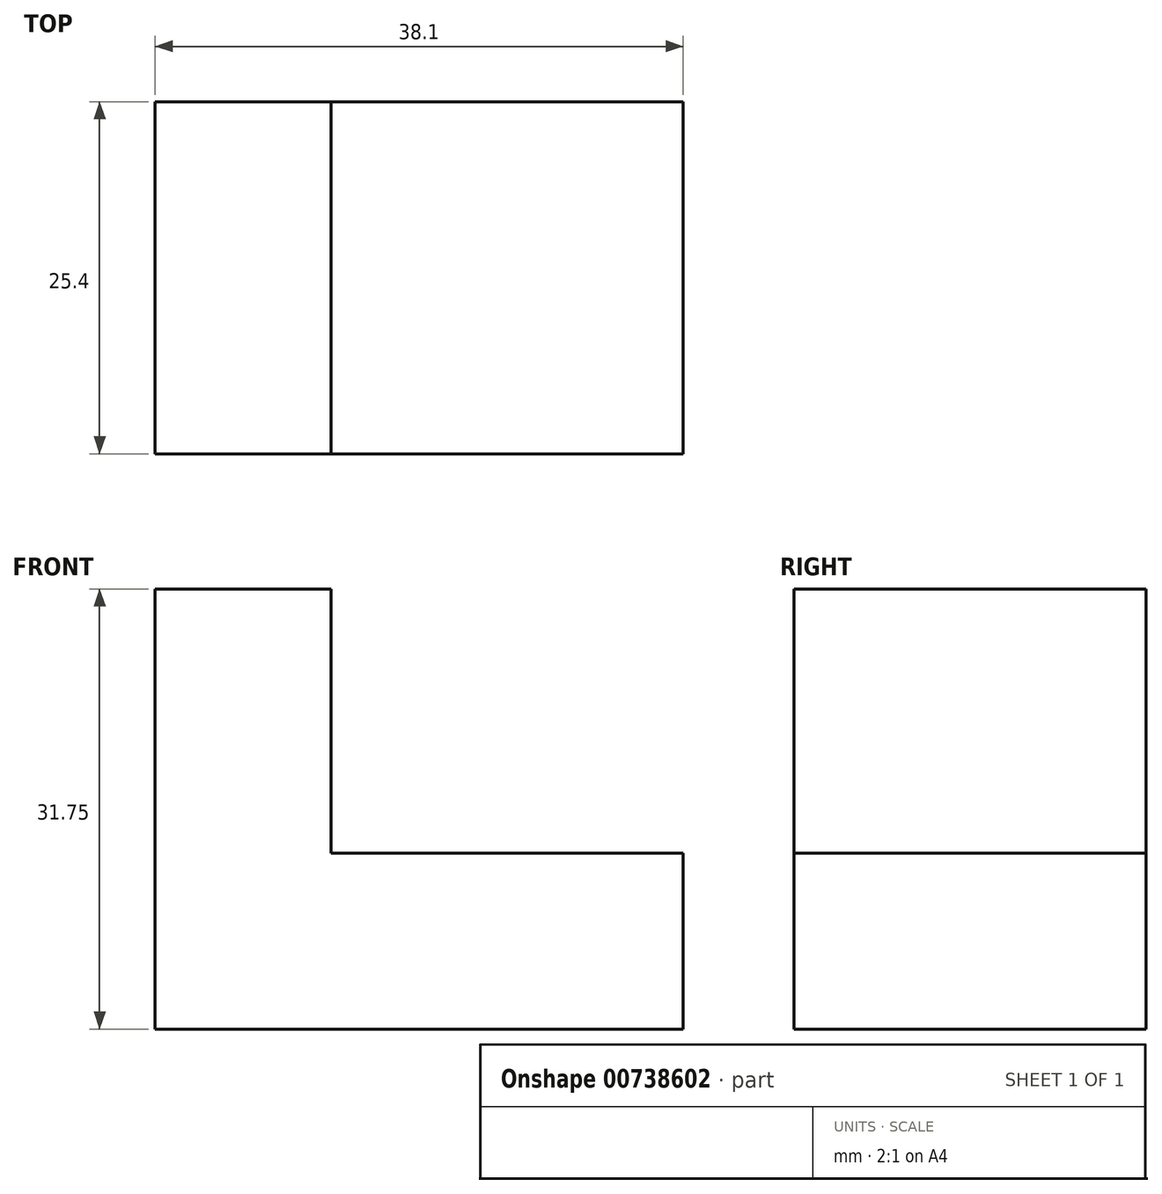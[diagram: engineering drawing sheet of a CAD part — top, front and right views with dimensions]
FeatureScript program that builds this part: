
annotation { "Feature Type Name" : "Feature", "Feature Type Description" : "" }
export const myFeature = defineFeature(function(context is Context, id is Id, definition is map)
    precondition{}
    {
        {
            var Q0;
            Q0=qCreatedBy(makeId("Front.planeOp"),FACE);
            var sketch = newSketch(context, id + "F0", { "sketchPlane" : qUnion([Q0])});
            skLineSegment(sketch, "E0", {"start": v(0, 31.75) * mm, "end": v(0, 0) * mm});
            skLineSegment(sketch, "E1", {"start": v(38.1, 0) * mm, "end": v(38.1, 12.7) * mm});
            skLineSegment(sketch, "E2", {"start": v(38.1, 12.7) * mm, "end": v(12.7, 12.7) * mm});
            skLineSegment(sketch, "E3", {"start": v(12.7, 12.7) * mm, "end": v(12.7, 31.75) * mm});
            skLineSegment(sketch, "E4", {"start": v(12.7, 31.75) * mm, "end": v(0, 31.75) * mm});
            skLineSegment(sketch, "E5", {"start": v(38.1, 0) * mm, "end": v(0, 0) * mm});
            skSolve(sketch);
        }
        {
            var Q0;
            Q0 = qSketchRegion(id + "F0", true);
            extrude(context, id + "F1", {"entities" : qUnion([Q0]), "depth" : 25.4 * mm, "offsetDistance" : 25.4 * mm});
        }
    });
